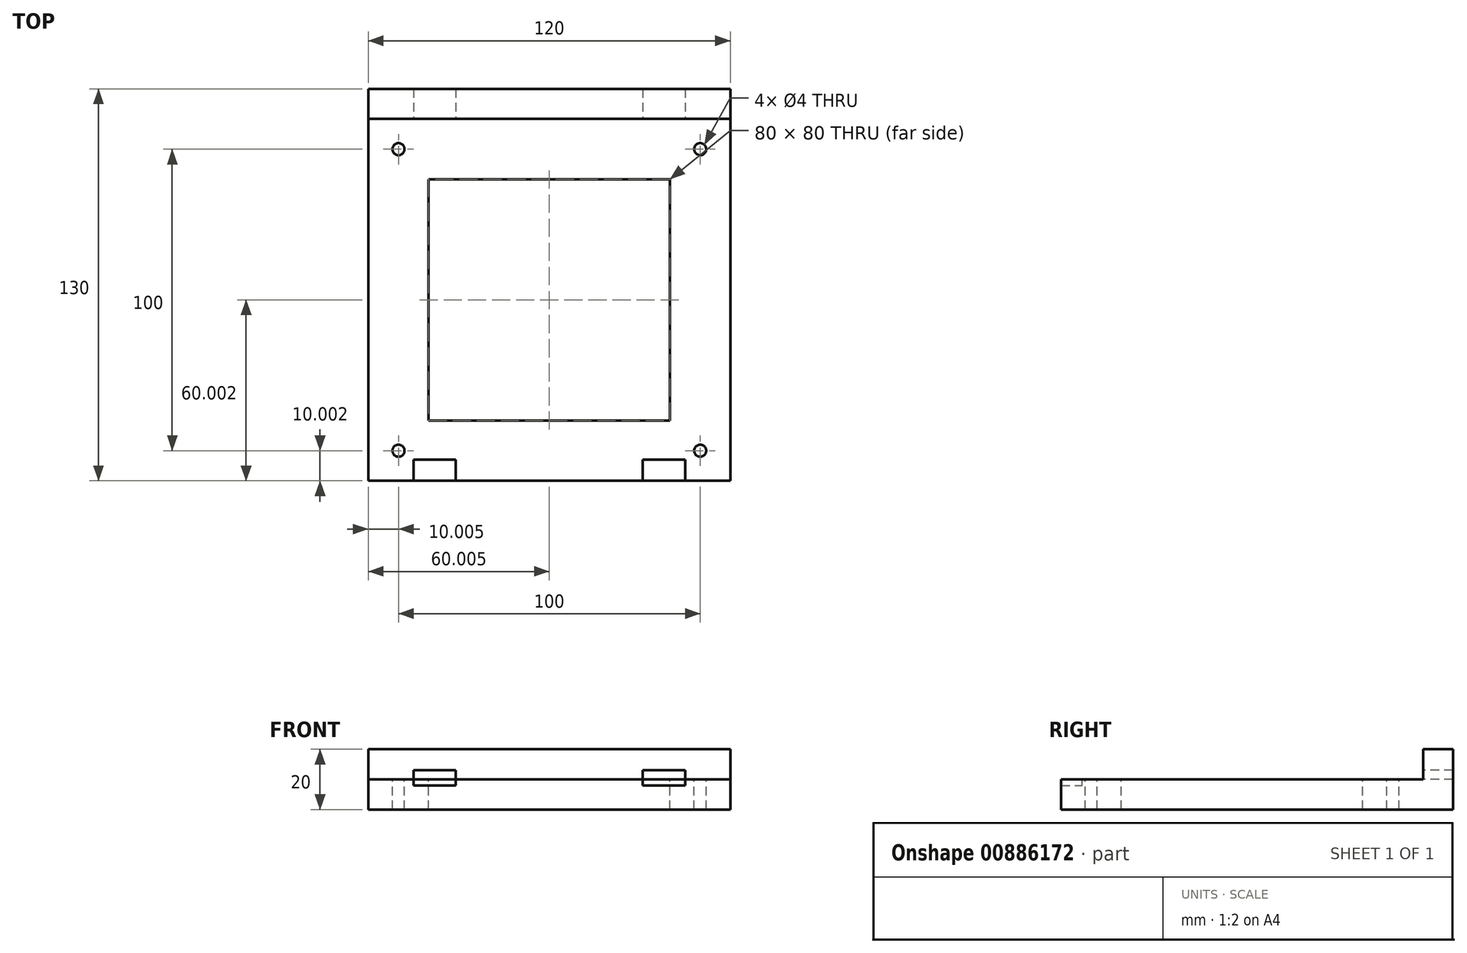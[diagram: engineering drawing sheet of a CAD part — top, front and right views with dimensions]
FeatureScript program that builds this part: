
annotation { "Feature Type Name" : "Feature", "Feature Type Description" : "" }
export const myFeature = defineFeature(function(context is Context, id is Id, definition is map)
    precondition{}
    {
        {
            var Q0;
            Q0=qCreatedBy(makeId("Top.planeOp"),FACE);
            var sketch = newSketch(context, id + "F0", { "sketchPlane" : qUnion([Q0])});
            skLineSegment(sketch, "E0.bottom", {"start": v(-58.02, 85.88) * mm, "end": v(61.98, 85.88) * mm});
            skLineSegment(sketch, "E0.top", {"start": v(-58.02, -44.12) * mm, "end": v(61.98, -44.12) * mm});
            skLineSegment(sketch, "E0.left", {"start": v(-58.02, 85.88) * mm, "end": v(-58.02, -44.12) * mm});
            skLineSegment(sketch, "E0.right", {"start": v(61.98, 85.88) * mm, "end": v(61.98, -44.12) * mm});
            skSolve(sketch);
        }
        {
            var Q0;
            Q0 = qSketchRegion(id + "F0", true);
            extrude(context, id + "F1", {"entities" : qUnion([Q0]), "depth" : 10 * mm, "offsetDistance" : 25 * mm});
        }
        {
            var Q0;
            Q0=makeQuery(id+"F1.opExtrude","CAP_FACE",FACE,{"disambiguationData":[OSD([sQuery(id+"F0.wireOp",EDGE,"E0.bottom"),sQuery(id+"F0.wireOp",EDGE,"E0.top"),sQuery(id+"F0.wireOp",EDGE,"E0.left"),sQuery(id+"F0.wireOp",EDGE,"E0.right")])],"isStart":false});
            var sketch = newSketch(context, id + "F2", { "sketchPlane" : qUnion([Q0])});
            skLineSegment(sketch, "E1", {"start": v(-58.02, 85.88) * mm, "end": v(-58.02, 75.88) * mm, "construction": true});
            skLineSegment(sketch, "E2", {"start": v(-58.02, 75.88) * mm, "end": v(61.98, 75.88) * mm});
            skSolve(sketch);
        }
        {
            var Q0;
            {var subQ0=sQuery(id+"F2.wireOp",EDGE,"E2");Q0=makeQuery(id+"F2.imprint","IMPRINT",FACE,{"disambiguationData":[TD([[makeQuery(id+"F2.imprint","IMPRINT",EDGE,{"derivedFrom":subQ0}),1.0]])]});}
            extrude(context, id + "F3", {"entities" : qUnion([Q0]), "operationType" : NewBodyOperationType.ADD, "depth" : 10 * mm, "offsetDistance" : 25 * mm});
        }
        {
            var Q0;
            Q0=makeQuery(id+"F3.opExtrude","SWEPT_FACE",FACE,{"disambiguationData":[OSD([sQuery(id+"F2.wireOp",EDGE,"E2")])]});
            var sketch = newSketch(context, id + "F4", { "sketchPlane" : qUnion([Q0])});
            skLineSegment(sketch, "E3.bottom", {"start": v(-58.02, 20) * mm, "end": v(-43.02, 20) * mm, "construction": true});
            skLineSegment(sketch, "E3.top", {"start": v(-58.02, 10) * mm, "end": v(-43.02, 10) * mm, "construction": true});
            skLineSegment(sketch, "E3.left", {"start": v(-58.02, 20) * mm, "end": v(-58.02, 10) * mm, "construction": true});
            skLineSegment(sketch, "E3.right", {"start": v(-43.02, 20) * mm, "end": v(-43.02, 10) * mm, "construction": true});
            skLineSegment(sketch, "E4.bottom", {"start": v(61.98, 20) * mm, "end": v(46.98, 20) * mm, "construction": true});
            skLineSegment(sketch, "E4.top", {"start": v(61.98, 10) * mm, "end": v(46.98, 10) * mm, "construction": true});
            skLineSegment(sketch, "E4.left", {"start": v(61.98, 20) * mm, "end": v(61.98, 10) * mm, "construction": true});
            skLineSegment(sketch, "E4.right", {"start": v(46.98, 20) * mm, "end": v(46.98, 10) * mm, "construction": true});
            skLineSegment(sketch, "E5.bottom", {"start": v(-58.02, 20) * mm, "end": v(-29.02, 20) * mm, "construction": true});
            skLineSegment(sketch, "E5.top", {"start": v(-58.02, 10) * mm, "end": v(-29.02, 10) * mm, "construction": true});
            skLineSegment(sketch, "E5.right", {"start": v(-29.02, 20) * mm, "end": v(-29.02, 10) * mm, "construction": true});
            skLineSegment(sketch, "E6.bottom", {"start": v(61.98, 20) * mm, "end": v(32.98, 20) * mm, "construction": true});
            skLineSegment(sketch, "E6.top", {"start": v(61.98, 10) * mm, "end": v(32.98, 10) * mm, "construction": true});
            skLineSegment(sketch, "E6.right", {"start": v(32.98, 20) * mm, "end": v(32.98, 10) * mm, "construction": true});
            skLineSegment(sketch, "E7.bottom", {"start": v(-29.02, 10) * mm, "end": v(-43.02, 10) * mm});
            skLineSegment(sketch, "E7.top", {"start": v(-29.02, 13) * mm, "end": v(-43.02, 13) * mm});
            skLineSegment(sketch, "E7.left", {"start": v(-29.02, 10) * mm, "end": v(-29.02, 13) * mm});
            skLineSegment(sketch, "E7.right", {"start": v(-43.02, 10) * mm, "end": v(-43.02, 13) * mm});
            skLineSegment(sketch, "E8.bottom", {"start": v(32.98, 10) * mm, "end": v(46.98, 10) * mm});
            skLineSegment(sketch, "E8.top", {"start": v(32.98, 13) * mm, "end": v(46.98, 13) * mm});
            skLineSegment(sketch, "E8.left", {"start": v(32.98, 10) * mm, "end": v(32.98, 13) * mm});
            skLineSegment(sketch, "E8.right", {"start": v(46.98, 10) * mm, "end": v(46.98, 13) * mm});
            skSolve(sketch);
        }
        {
            var Q0;
            Q0=makeQuery(id+"F4.imprint","IMPRINT",FACE,{"disambiguationData":[TD([[makeQuery(id+"F4.imprint","IMPRINT",EDGE,{"derivedFrom":sQuery(id+"F4.wireOp",EDGE,"E7.bottom")}),1.0]])]});
            extrude(context, id + "F5", {"entities" : qUnion([Q0]), "operationType" : NewBodyOperationType.REMOVE, "oppositeDirection" : true, "depth" : 25 * mm, "offsetDistance" : 25 * mm});
        }
        {
            var Q0;
            Q0=makeQuery(id+"F4.imprint","IMPRINT",FACE,{"disambiguationData":[TD([[makeQuery(id+"F4.imprint","IMPRINT",EDGE,{"derivedFrom":sQuery(id+"F4.wireOp",EDGE,"E8.bottom")}),1.0]])]});
            extrude(context, id + "F6", {"entities" : qUnion([Q0]), "operationType" : NewBodyOperationType.REMOVE, "oppositeDirection" : true, "depth" : 25 * mm, "offsetDistance" : 25 * mm});
        }
        {
            var Q0;
            Q0=makeQuery(id+"F6.boolean.opBoolean","MERGE",FACE,{"derivedFrom":[makeQuery(id+"F5.boolean.opBoolean","MERGE",FACE,{"derivedFrom":[makeQuery(id+"F1.opExtrude","CAP_FACE",FACE,{"disambiguationData":[OSD([sQuery(id+"F0.wireOp",EDGE,"E0.bottom"),sQuery(id+"F0.wireOp",EDGE,"E0.top"),sQuery(id+"F0.wireOp",EDGE,"E0.left"),sQuery(id+"F0.wireOp",EDGE,"E0.right")])],"isStart":false})],"fromTools":[makeQuery(id+"F5.opExtrude","SWEPT_FACE",FACE,{"disambiguationData":[OSD([sQuery(id+"F4.wireOp",EDGE,"E7.bottom")])]})]})],"fromTools":[makeQuery(id+"F6.opExtrude","SWEPT_FACE",FACE,{"disambiguationData":[OSD([sQuery(id+"F4.wireOp",EDGE,"E8.bottom")])]})]});
            var sketch = newSketch(context, id + "F7", { "sketchPlane" : qUnion([Q0])});
            skLineSegment(sketch, "E9.bottom", {"start": v(-48.02, -34.12) * mm, "end": v(51.98, -34.12) * mm, "construction": true});
            skLineSegment(sketch, "E9.top", {"start": v(-48.02, 65.88) * mm, "end": v(51.98, 65.88) * mm, "construction": true});
            skLineSegment(sketch, "E9.left", {"start": v(-48.02, -34.12) * mm, "end": v(-48.02, 65.88) * mm, "construction": true});
            skLineSegment(sketch, "E9.right", {"start": v(51.98, -34.12) * mm, "end": v(51.98, 65.88) * mm, "construction": true});
            skLineSegment(sketch, "E10", {"start": v(-58.02, 75.88) * mm, "end": v(61.98, -44.12) * mm, "construction": true});
            skLineSegment(sketch, "E11", {"start": v(61.98, -44.12) * mm, "end": v(61.98, 75.88) * mm, "construction": true});
            skLineSegment(sketch, "E12", {"start": v(61.98, 75.88) * mm, "end": v(-58.02, -44.12) * mm, "construction": true});
            skLineSegment(sketch, "E13", {"start": v(-48.02, 65.88) * mm, "end": v(51.98, -34.12) * mm, "construction": true});
            skLineSegment(sketch, "E14", {"start": v(51.98, 65.88) * mm, "end": v(-48.02, -34.12) * mm, "construction": true});
            skPoint(sketch, "E15", {"position": v(1.98, 15.88) * mm});
            skCircle(sketch, "E16", {"center": v(-48.02, 65.88) * mm, "radius": 2 * mm});
            skCircle(sketch, "E17", {"center": v(51.98, 65.88) * mm, "radius": 2 * mm});
            skCircle(sketch, "E18", {"center": v(51.98, -34.12) * mm, "radius": 2 * mm});
            skCircle(sketch, "E19", {"center": v(-48.02, -34.12) * mm, "radius": 2 * mm});
            skSolve(sketch);
        }
        {
            var Q0;
            Q0=makeQuery(id+"F7.imprint","IMPRINT",FACE,{"disambiguationData":[TD([[makeQuery(id+"F7.imprint","IMPRINT",EDGE,{"derivedFrom":sQuery(id+"F7.wireOp",EDGE,"E16")}),1.0]])]});
            var Q1;
            Q1=makeQuery(id+"F7.imprint","IMPRINT",FACE,{"disambiguationData":[TD([[makeQuery(id+"F7.imprint","IMPRINT",EDGE,{"derivedFrom":sQuery(id+"F7.wireOp",EDGE,"E17")}),1.0]])]});
            var Q2;
            Q2=makeQuery(id+"F7.imprint","IMPRINT",FACE,{"disambiguationData":[TD([[makeQuery(id+"F7.imprint","IMPRINT",EDGE,{"derivedFrom":sQuery(id+"F7.wireOp",EDGE,"E18")}),1.0]])]});
            var Q3;
            Q3=makeQuery(id+"F7.imprint","IMPRINT",FACE,{"disambiguationData":[TD([[makeQuery(id+"F7.imprint","IMPRINT",EDGE,{"derivedFrom":sQuery(id+"F7.wireOp",EDGE,"E19")}),1.0]])]});
            extrude(context, id + "F8", {"entities" : qUnion([Q0, Q1, Q2, Q3]), "operationType" : NewBodyOperationType.REMOVE, "oppositeDirection" : true, "depth" : 25 * mm, "offsetDistance" : 25 * mm});
        }
        {
            var Q0;
            Q0=makeQuery(id+"F6.boolean.opBoolean","MERGE",FACE,{"derivedFrom":[makeQuery(id+"F5.boolean.opBoolean","MERGE",FACE,{"derivedFrom":[makeQuery(id+"F1.opExtrude","CAP_FACE",FACE,{"disambiguationData":[OSD([sQuery(id+"F0.wireOp",EDGE,"E0.bottom"),sQuery(id+"F0.wireOp",EDGE,"E0.top"),sQuery(id+"F0.wireOp",EDGE,"E0.left"),sQuery(id+"F0.wireOp",EDGE,"E0.right")])],"isStart":false})],"fromTools":[makeQuery(id+"F5.opExtrude","SWEPT_FACE",FACE,{"disambiguationData":[OSD([sQuery(id+"F4.wireOp",EDGE,"E7.bottom")])]})]})],"fromTools":[makeQuery(id+"F6.opExtrude","SWEPT_FACE",FACE,{"disambiguationData":[OSD([sQuery(id+"F4.wireOp",EDGE,"E8.bottom")])]})]});
            var sketch = newSketch(context, id + "F9", { "sketchPlane" : qUnion([Q0])});
            skLineSegment(sketch, "E20", {"start": v(-43.02, 75.88) * mm, "end": v(-43.02, -44.12) * mm, "construction": true});
            skLineSegment(sketch, "E21", {"start": v(-29.02, 75.88) * mm, "end": v(-29.02, -44.12) * mm, "construction": true});
            skLineSegment(sketch, "E22", {"start": v(32.98, 75.88) * mm, "end": v(32.98, -44.12) * mm, "construction": true});
            skLineSegment(sketch, "E23", {"start": v(46.98, 75.88) * mm, "end": v(46.98, -44.12) * mm, "construction": true});
            skLineSegment(sketch, "E24.bottom", {"start": v(-43.02, -44.12) * mm, "end": v(-29.02, -44.12) * mm});
            skLineSegment(sketch, "E24.top", {"start": v(-43.02, -37.12) * mm, "end": v(-29.02, -37.12) * mm});
            skLineSegment(sketch, "E24.left", {"start": v(-43.02, -44.12) * mm, "end": v(-43.02, -37.12) * mm});
            skLineSegment(sketch, "E24.right", {"start": v(-29.02, -44.12) * mm, "end": v(-29.02, -37.12) * mm});
            skLineSegment(sketch, "E25.bottom", {"start": v(32.98, -44.12) * mm, "end": v(46.98, -44.12) * mm});
            skLineSegment(sketch, "E25.top", {"start": v(32.98, -37.12) * mm, "end": v(46.98, -37.12) * mm});
            skLineSegment(sketch, "E25.left", {"start": v(32.98, -44.12) * mm, "end": v(32.98, -37.12) * mm});
            skLineSegment(sketch, "E25.right", {"start": v(46.98, -44.12) * mm, "end": v(46.98, -37.12) * mm});
            skSolve(sketch);
        }
        {
            var Q0;
            Q0=makeQuery(id+"F9.imprint","IMPRINT",FACE,{"disambiguationData":[TD([[makeQuery(id+"F9.imprint","IMPRINT",EDGE,{"derivedFrom":sQuery(id+"F9.wireOp",EDGE,"E24.bottom")}),1.0]])]});
            var Q1;
            Q1=makeQuery(id+"F9.imprint","IMPRINT",FACE,{"disambiguationData":[TD([[makeQuery(id+"F9.imprint","IMPRINT",EDGE,{"derivedFrom":sQuery(id+"F9.wireOp",EDGE,"E25.bottom")}),1.0]])]});
            extrude(context, id + "F10", {"entities" : qUnion([Q0, Q1]), "operationType" : NewBodyOperationType.REMOVE, "oppositeDirection" : true, "depth" : 2 * mm, "offsetDistance" : 25 * mm});
        }
        {
            var Q0;
            Q0=makeQuery(id+"F6.boolean.opBoolean","MERGE",FACE,{"derivedFrom":[makeQuery(id+"F5.boolean.opBoolean","MERGE",FACE,{"derivedFrom":[makeQuery(id+"F1.opExtrude","CAP_FACE",FACE,{"disambiguationData":[OSD([sQuery(id+"F0.wireOp",EDGE,"E0.bottom"),sQuery(id+"F0.wireOp",EDGE,"E0.top"),sQuery(id+"F0.wireOp",EDGE,"E0.left"),sQuery(id+"F0.wireOp",EDGE,"E0.right")])],"isStart":false})],"fromTools":[makeQuery(id+"F5.opExtrude","SWEPT_FACE",FACE,{"disambiguationData":[OSD([sQuery(id+"F4.wireOp",EDGE,"E7.bottom")])]})]})],"fromTools":[makeQuery(id+"F6.opExtrude","SWEPT_FACE",FACE,{"disambiguationData":[OSD([sQuery(id+"F4.wireOp",EDGE,"E8.bottom")])]})]});
            var sketch = newSketch(context, id + "F11", { "sketchPlane" : qUnion([Q0])});
            skLineSegment(sketch, "E26.0", {"start": v(-38.02, 55.88) * mm, "end": v(41.98, 55.88) * mm});
            skLineSegment(sketch, "E26.1", {"start": v(-38.02, -24.12) * mm, "end": v(-38.02, 55.88) * mm});
            skLineSegment(sketch, "E26.2", {"start": v(-38.02, -24.12) * mm, "end": v(41.98, -24.12) * mm});
            skLineSegment(sketch, "E26.3", {"start": v(41.98, -24.12) * mm, "end": v(41.98, 55.88) * mm});
            skSolve(sketch);
        }
        {
            var Q0;
            Q0=makeQuery(id+"F11.imprint","IMPRINT",FACE,{"disambiguationData":[TD([[makeQuery(id+"F11.imprint","IMPRINT",EDGE,{"derivedFrom":sQuery(id+"F11.wireOp",EDGE,"E26.0")}),-1.0]])]});
            extrude(context, id + "F12", {"entities" : qUnion([Q0]), "operationType" : NewBodyOperationType.REMOVE, "oppositeDirection" : true, "depth" : 25 * mm, "offsetDistance" : 25 * mm});
        }
    });
